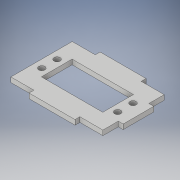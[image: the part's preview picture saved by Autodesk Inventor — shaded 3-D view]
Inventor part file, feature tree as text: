
AUTODESK INVENTOR PART (.ipt)
format: ipt  version: 2019 (Build 230136000, 136)  size: 142,336 bytes
history: native  units: mm
features: other x1, extrude x1, sketch x1
ambient origin geometry x8: Origin, YZ Plane, XZ Plane, XY Plane, X Axis, Y Axis, Z Axis, Center Point
bodies: Body1 (feature_tree)
feature tree (3):
  other  "Sólido1"
  extrude  "Extrusión1"  Depth=40.0mm
  sketch  "Boceto1"  dims[d0=10.0mm d1=10.0mm d2=20.0mm d3=10.1mm d4=40.0mm d5=4.0mm d6=4.0mm d7=4.0mm d8=5.0mm d9=10.0mm d10=14.85mm d11=14.85mm d12=4.0mm d13=34.66mm d14=34.66mm d15=5.0mm d16=10.0mm d25=40.0mm d26=60.0mm d27=20.0mm d28=20.0mm d29=3.18mm d30=30.0mm d31=15.0mm d32=20.0mm d33=10.0mm d34=3.18mm d35=3.18mm d36=0.0mm]
